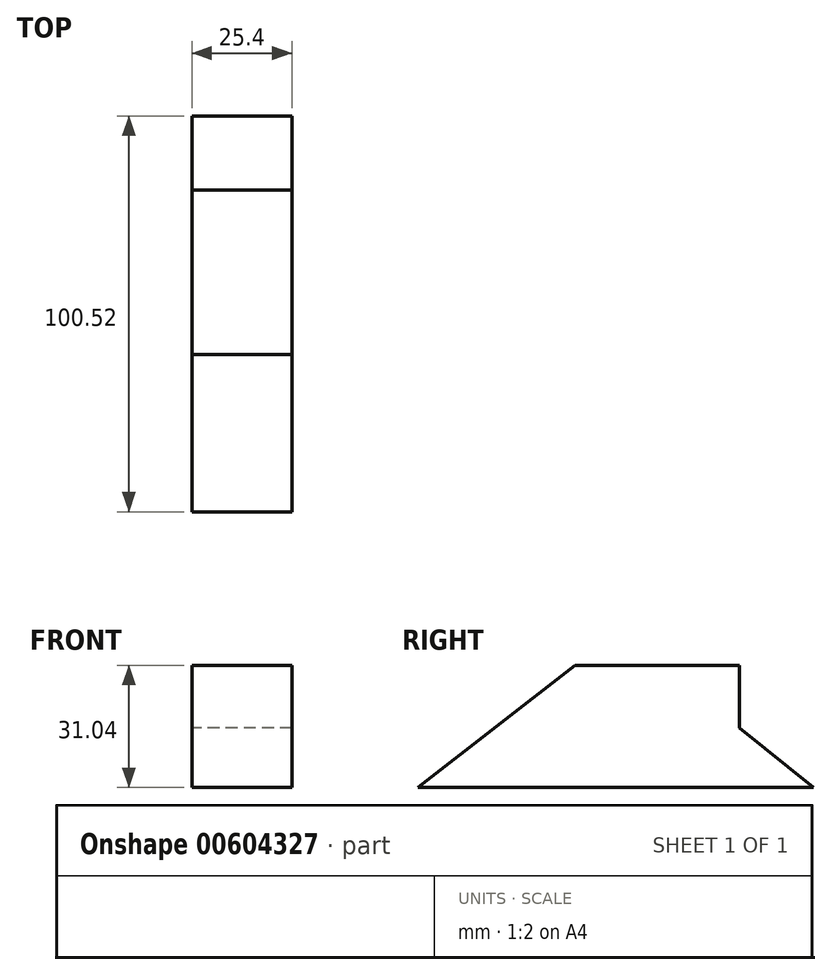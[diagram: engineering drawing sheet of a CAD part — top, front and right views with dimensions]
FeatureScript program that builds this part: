
annotation { "Feature Type Name" : "Feature", "Feature Type Description" : "" }
export const myFeature = defineFeature(function(context is Context, id is Id, definition is map)
    precondition{}
    {
        {
            var Q0;
            Q0=qCreatedBy(makeId("Right.planeOp"),FACE);
            var sketch = newSketch(context, id + "F0", { "sketchPlane" : qUnion([Q0])});
            skLineSegment(sketch, "E0", {"start": v(0, 0) * mm, "end": v(-39.91, 0) * mm});
            skLineSegment(sketch, "E1", {"start": v(-39.91, 0) * mm, "end": v(0, 31.04) * mm});
            skLineSegment(sketch, "E2", {"start": v(0, 31.04) * mm, "end": v(41.76, 31.04) * mm});
            skLineSegment(sketch, "E3", {"start": v(41.76, 31.04) * mm, "end": v(41.76, 15.15) * mm});
            skLineSegment(sketch, "E4", {"start": v(41.76, 15.15) * mm, "end": v(60.6, 0) * mm});
            skLineSegment(sketch, "E5", {"start": v(-39.91, 0) * mm, "end": v(60.6, 0) * mm});
            skSolve(sketch);
        }
        {
            var Q0;
            Q0 = qSketchRegion(id + "F0", true);
            extrude(context, id + "F1", {"entities" : qUnion([Q0]), "depth" : 25.4 * mm, "offsetDistance" : 25.4 * mm});
        }
    });
